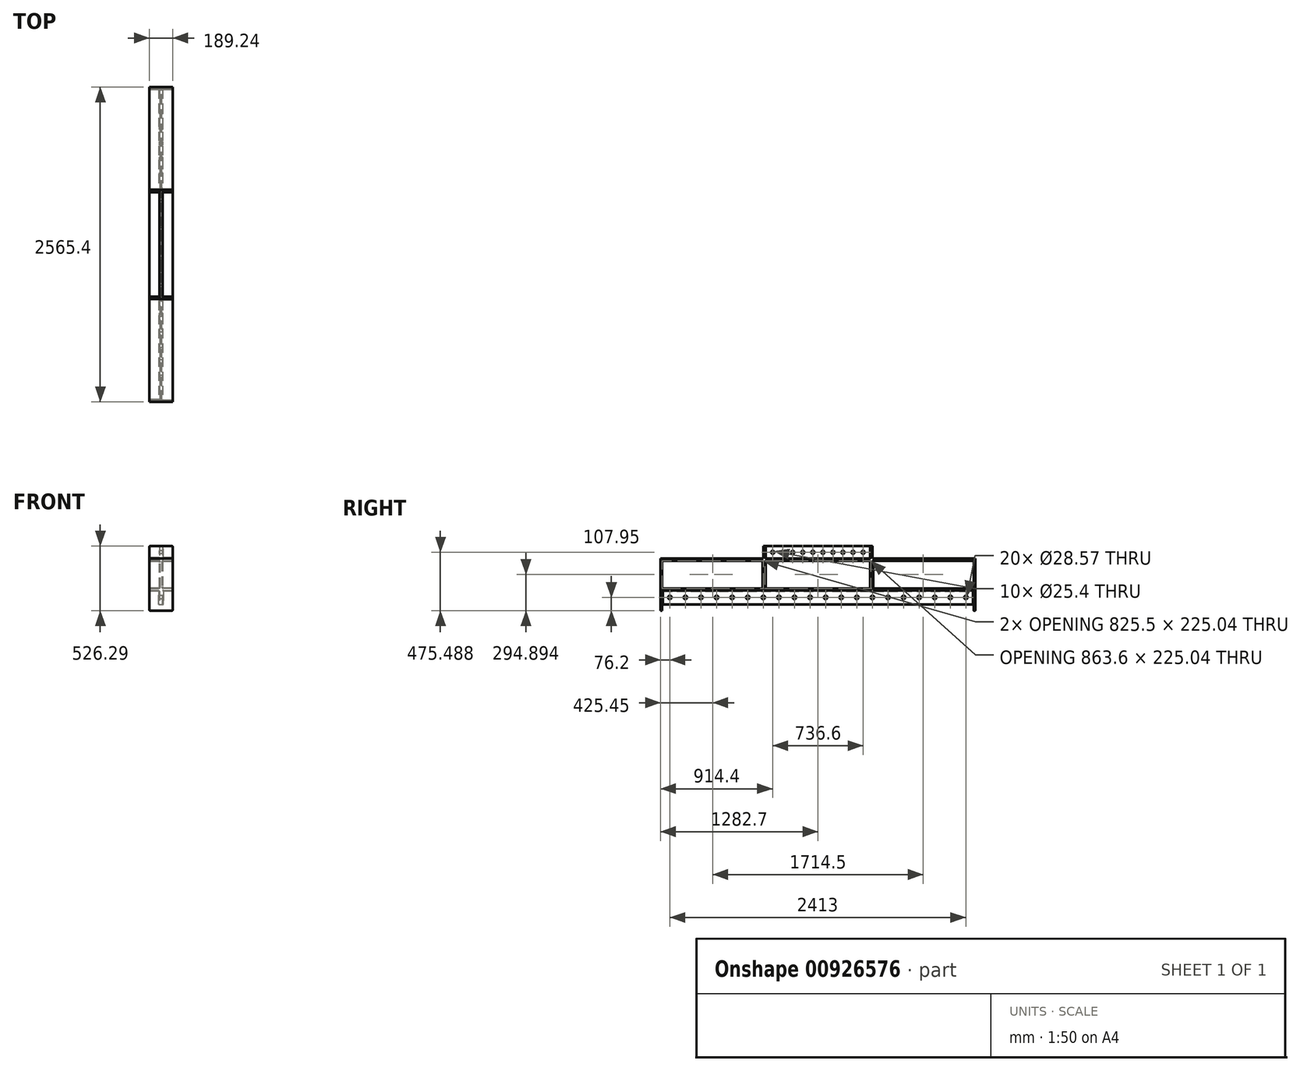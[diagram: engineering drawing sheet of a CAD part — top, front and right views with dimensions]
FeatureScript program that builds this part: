
annotation { "Feature Type Name" : "Feature", "Feature Type Description" : "" }
export const myFeature = defineFeature(function(context is Context, id is Id, definition is map)
    precondition{}
    {
        {
            var Q0;
            Q0=qCreatedBy(makeId("Front.planeOp"),FACE);
            var sketch = newSketch(context, id + "F0", { "sketchPlane" : qUnion([Q0])});
            skLineSegment(sketch, "E0", {"start": v(0, 0) * mm, "end": v(0, 259.59) * mm, "construction": true});
            skLineSegment(sketch, "E1", {"start": v(-94.62, 0) * mm, "end": v(94.62, 0) * mm, "construction": true});
            skLineSegment(sketch, "E2", {"start": v(-94.61, 259.59) * mm, "end": v(94.61, 259.59) * mm, "construction": true});
            skLineSegment(sketch, "E3", {"start": v(-94.61, 259.59) * mm, "end": v(94.61, 259.59) * mm});
            skLineSegment(sketch, "E4", {"start": v(-94.62, 0) * mm, "end": v(94.62, 0) * mm});
            skLineSegment(sketch, "E5", {"start": v(94.62, 17.27) * mm, "end": v(94.62, 0) * mm});
            skLineSegment(sketch, "E6", {"start": v(-94.62, 0) * mm, "end": v(-94.62, 17.27) * mm});
            skLineSegment(sketch, "E7", {"start": v(-94.61, 259.59) * mm, "end": v(-94.61, 242.32) * mm});
            skLineSegment(sketch, "E8", {"start": v(94.62, 259.59) * mm, "end": v(94.62, 242.32) * mm});
            skLineSegment(sketch, "E9", {"start": v(-94.62, 242.32) * mm, "end": v(-18.22, 242.32) * mm});
            skLineSegment(sketch, "E10", {"start": v(94.62, 242.32) * mm, "end": v(18.22, 242.32) * mm});
            skLineSegment(sketch, "E11", {"start": v(94.62, 17.27) * mm, "end": v(18.22, 17.27) * mm});
            skLineSegment(sketch, "E12", {"start": v(-94.62, 17.27) * mm, "end": v(-18.22, 17.27) * mm});
            skLineSegment(sketch, "E13", {"start": v(-5.33, 229.43) * mm, "end": v(-5.33, 30.16) * mm});
            skLineSegment(sketch, "E14", {"start": v(5.33, 229.43) * mm, "end": v(5.33, 30.16) * mm});
            skLineSegment(sketch, "E15", {"start": v(-5.33, 242.32) * mm, "end": v(5.33, 242.32) * mm, "construction": true});
            skPoint(sketch, "E16", {"position": v(0, 242.32) * mm});
            skPoint(sketch, "E17.visualSharp", {"position": v(-5.33, 242.32) * mm});
            skArc(sketch, "E17.filletArc", {"start": v(-5.33, 229.43) * mm, "mid": v(-9.1, 238.54) * mm, "end": v(-18.22, 242.32) * mm});
            skPoint(sketch, "E18.visualSharp", {"position": v(5.33, 242.32) * mm});
            skArc(sketch, "E18.filletArc", {"start": v(18.22, 242.32) * mm, "mid": v(9.1, 238.54) * mm, "end": v(5.33, 229.43) * mm});
            skPoint(sketch, "E19.visualSharp", {"position": v(5.33, 17.27) * mm});
            skArc(sketch, "E19.filletArc", {"start": v(5.33, 30.16) * mm, "mid": v(9.1, 21.05) * mm, "end": v(18.22, 17.27) * mm});
            skPoint(sketch, "E20.visualSharp", {"position": v(-5.33, 17.27) * mm});
            skArc(sketch, "E20.filletArc", {"start": v(-18.22, 17.27) * mm, "mid": v(-9.1, 21.05) * mm, "end": v(-5.33, 30.16) * mm});
            skSolve(sketch);
        }
        {
            var Q0;
            Q0=makeQuery(id+"F0.imprint","IMPRINT",FACE,{"disambiguationData":[TD([[makeQuery(id+"F0.imprint","IMPRINT",EDGE,{"derivedFrom":sQuery(id+"F0.wireOp",EDGE,"E3")}),-1.0]])]});
            extrude(context, id + "F1", {"entities" : qUnion([Q0]), "depth" : 2540 * mm, "offsetDistance" : 25.4 * mm});
        }
        {
            var Q0;
            Q0=qCreatedBy(makeId("Right.planeOp"),FACE);
            var sketch = newSketch(context, id + "F2", { "sketchPlane" : qUnion([Q0])});
            skPoint(sketch, "E21.0", {"position": v(-1270, 259.59) * mm});
            skLineSegment(sketch, "E22", {"start": v(-1270, 259.59) * mm, "end": v(-1270, 361.19) * mm, "construction": true});
            skLineSegment(sketch, "E23", {"start": v(-838.2, 361.19) * mm, "end": v(-1701.8, 361.19) * mm});
            skPoint(sketch, "E24", {"position": v(-1270, 310.39) * mm});
            skLineSegment(sketch, "E25", {"start": v(-838.2, 361.19) * mm, "end": v(-838.2, 259.59) * mm});
            skLineSegment(sketch, "E26", {"start": v(-838.2, 259.59) * mm, "end": v(-1701.8, 259.59) * mm});
            skLineSegment(sketch, "E27", {"start": v(-1701.8, 259.59) * mm, "end": v(-1701.8, 361.19) * mm});
            skPoint(sketch, "E28.visualSharp", {"position": v(-1701.8, 361.19) * mm});
            skPoint(sketch, "E29.visualSharp", {"position": v(-838.2, 361.19) * mm});
            skLineSegment(sketch, "E30", {"start": v(-901.7, 310.39) * mm, "end": v(-1638.3, 310.39) * mm, "construction": true});
            skCircle(sketch, "E31", {"center": v(-901.7, 310.39) * mm, "radius": 12.7 * mm});
            skCircle(sketch, "E32.1.0.0", {"center": v(-983.54, 310.39) * mm, "radius": 12.7 * mm});
            skCircle(sketch, "E32.2.0.0", {"center": v(-1065.39, 310.39) * mm, "radius": 12.7 * mm});
            skCircle(sketch, "E32.3.0.0", {"center": v(-1147.23, 310.39) * mm, "radius": 12.7 * mm});
            skCircle(sketch, "E32.4.0.0", {"center": v(-1229.08, 310.39) * mm, "radius": 12.7 * mm});
            skCircle(sketch, "E32.5.0.0", {"center": v(-1310.92, 310.39) * mm, "radius": 12.7 * mm});
            skCircle(sketch, "E32.6.0.0", {"center": v(-1392.77, 310.39) * mm, "radius": 12.7 * mm});
            skCircle(sketch, "E32.7.0.0", {"center": v(-1474.61, 310.39) * mm, "radius": 12.7 * mm});
            skCircle(sketch, "E32.8.0.0", {"center": v(-1556.46, 310.39) * mm, "radius": 12.7 * mm});
            skCircle(sketch, "E32.9.0.0", {"center": v(-1638.3, 310.39) * mm, "radius": 12.7 * mm});
            skLineSegment(sketch, "E32.direction1", {"start": v(-901.7, 310.39) * mm, "end": v(-983.54, 310.39) * mm, "construction": true});
            skLineSegment(sketch, "E33", {"start": v(-901.7, 310.39) * mm, "end": v(-901.7, 323.09) * mm, "construction": true});
            skSolve(sketch);
        }
        {
            var Q0;
            Q0=makeQuery(id+"F2.imprint","IMPRINT",FACE,{"disambiguationData":[TD([[makeQuery(id+"F2.imprint","IMPRINT",EDGE,{"derivedFrom":sQuery(id+"F2.wireOp",EDGE,"E23")}),1.0]])]});
            extrude(context, id + "F3", {"entities" : qUnion([Q0]), "operationType" : NewBodyOperationType.ADD, "depth" : 12.7 * mm, "offsetDistance" : 25.4 * mm, "hasSecondDirection" : true, "secondDirectionOppositeDirection" : true, "secondDirectionDepth" : 12.7 * mm});
        }
        {
            var Q0;
            Q0=qCreatedBy(makeId("Right.planeOp"),FACE);
            var sketch = newSketch(context, id + "F4", { "sketchPlane" : qUnion([Q0])});
            skLineSegment(sketch, "E34.0", {"start": v(-2540, 0) * mm, "end": v(0, 0) * mm});
            skLineSegment(sketch, "E35", {"start": v(0, 0) * mm, "end": v(0, -114.3) * mm});
            skLineSegment(sketch, "E36", {"start": v(-2540, 0) * mm, "end": v(-2540, -114.3) * mm});
            skLineSegment(sketch, "E37", {"start": v(0, -114.3) * mm, "end": v(-2540, -114.3) * mm});
            skLineSegment(sketch, "E38", {"start": v(0, -57.15) * mm, "end": v(-2540, -57.15) * mm, "construction": true});
            skCircle(sketch, "E39", {"center": v(-63.5, -57.15) * mm, "radius": 14.29 * mm});
            skLineSegment(sketch, "E40", {"start": v(-63.5, -57.15) * mm, "end": v(-63.5, -71.44) * mm, "construction": true});
            skCircle(sketch, "E41.1.0.0", {"center": v(-190.5, -57.15) * mm, "radius": 14.29 * mm});
            skCircle(sketch, "E41.2.0.0", {"center": v(-317.5, -57.15) * mm, "radius": 14.29 * mm});
            skCircle(sketch, "E41.3.0.0", {"center": v(-444.5, -57.15) * mm, "radius": 14.29 * mm});
            skCircle(sketch, "E41.4.0.0", {"center": v(-571.5, -57.15) * mm, "radius": 14.29 * mm});
            skCircle(sketch, "E41.5.0.0", {"center": v(-698.5, -57.15) * mm, "radius": 14.29 * mm});
            skCircle(sketch, "E41.6.0.0", {"center": v(-825.5, -57.15) * mm, "radius": 14.29 * mm});
            skCircle(sketch, "E41.7.0.0", {"center": v(-952.5, -57.15) * mm, "radius": 14.29 * mm});
            skCircle(sketch, "E41.8.0.0", {"center": v(-1079.5, -57.15) * mm, "radius": 14.29 * mm});
            skCircle(sketch, "E41.9.0.0", {"center": v(-1206.5, -57.15) * mm, "radius": 14.29 * mm});
            skCircle(sketch, "E41.10.0.0", {"center": v(-1333.5, -57.15) * mm, "radius": 14.29 * mm});
            skCircle(sketch, "E41.11.0.0", {"center": v(-1460.5, -57.15) * mm, "radius": 14.29 * mm});
            skCircle(sketch, "E41.12.0.0", {"center": v(-1587.5, -57.15) * mm, "radius": 14.29 * mm});
            skCircle(sketch, "E41.13.0.0", {"center": v(-1714.5, -57.15) * mm, "radius": 14.29 * mm});
            skCircle(sketch, "E41.14.0.0", {"center": v(-1841.5, -57.15) * mm, "radius": 14.29 * mm});
            skCircle(sketch, "E41.15.0.0", {"center": v(-1968.5, -57.15) * mm, "radius": 14.29 * mm});
            skCircle(sketch, "E41.16.0.0", {"center": v(-2095.5, -57.15) * mm, "radius": 14.29 * mm});
            skCircle(sketch, "E41.17.0.0", {"center": v(-2222.5, -57.15) * mm, "radius": 14.29 * mm});
            skCircle(sketch, "E41.18.0.0", {"center": v(-2349.5, -57.15) * mm, "radius": 14.29 * mm});
            skCircle(sketch, "E41.19.0.0", {"center": v(-2476.5, -57.15) * mm, "radius": 14.29 * mm});
            skLineSegment(sketch, "E41.direction1", {"start": v(-63.5, -57.15) * mm, "end": v(-190.5, -57.15) * mm, "construction": true});
            skPoint(sketch, "E42.visualSharp", {"position": v(0, -114.3) * mm});
            skPoint(sketch, "E43.visualSharp", {"position": v(-2540, -114.3) * mm});
            skSolve(sketch);
        }
        {
            var Q0;
            Q0 = qSketchRegion(id + "F4", true);
            extrude(context, id + "F5", {"entities" : qUnion([Q0]), "operationType" : NewBodyOperationType.ADD, "depth" : 12.7 * mm, "offsetDistance" : 25.4 * mm, "hasSecondDirection" : true, "secondDirectionOppositeDirection" : true, "secondDirectionDepth" : 12.7 * mm});
        }
        {
            var Q0;
            Q0=makeQuery(id+"F5.boolean.opBoolean","MERGE",FACE,{"derivedFrom":[makeQuery(id+"F1.opExtrude","CAP_FACE",FACE,{"disambiguationData":[OSD([sQuery(id+"F0.wireOp",EDGE,"E3"),sQuery(id+"F0.wireOp",EDGE,"E4"),sQuery(id+"F0.wireOp",EDGE,"E5"),sQuery(id+"F0.wireOp",EDGE,"E6"),sQuery(id+"F0.wireOp",EDGE,"E7"),sQuery(id+"F0.wireOp",EDGE,"E8"),sQuery(id+"F0.wireOp",EDGE,"E9"),sQuery(id+"F0.wireOp",EDGE,"E10"),sQuery(id+"F0.wireOp",EDGE,"E11"),sQuery(id+"F0.wireOp",EDGE,"E12"),sQuery(id+"F0.wireOp",EDGE,"E13"),sQuery(id+"F0.wireOp",EDGE,"E14"),sQuery(id+"F0.wireOp",EDGE,"E17.filletArc"),sQuery(id+"F0.wireOp",EDGE,"E18.filletArc"),sQuery(id+"F0.wireOp",EDGE,"E19.filletArc"),sQuery(id+"F0.wireOp",EDGE,"E20.filletArc")])],"isStart":true}),makeQuery(id+"F5.opExtrude","SWEPT_FACE",FACE,{"disambiguationData":[OSD([sQuery(id+"F4.wireOp",EDGE,"E35")])]})]});
            var sketch = newSketch(context, id + "F6", { "sketchPlane" : qUnion([Q0])});
            skLineSegment(sketch, "E44.bottom", {"start": v(-94.61, 259.59) * mm, "end": v(94.61, 259.59) * mm});
            skLineSegment(sketch, "E44.top", {"start": v(-94.61, -114.3) * mm, "end": v(94.61, -114.3) * mm});
            skLineSegment(sketch, "E44.left", {"start": v(-94.61, 259.59) * mm, "end": v(-94.61, -114.3) * mm});
            skLineSegment(sketch, "E44.right", {"start": v(94.61, 259.59) * mm, "end": v(94.61, -114.3) * mm});
            skSolve(sketch);
        }
        {
            var Q0;
            {var subQ1=sQuery(id+"F4.wireOp",EDGE,"E35");var subQ2=makeQuery(id+"F5.opExtrude","CAP_EDGE",EDGE,{"disambiguationData":[OSD([subQ1])],"isStart":true});Q0=makeQuery(id+"F6.imprint","IMPRINT",FACE,{"disambiguationData":[TD([[makeQuery(id+"F6.imprint","IMPRINT",EDGE,{"derivedFrom":subQ2}),1.0]])]});}
            var Q1;
            {var subQ0=makeQuery(id+"F1.opExtrude","CAP_EDGE",EDGE,{"disambiguationData":[OSD([sQuery(id+"F0.wireOp",EDGE,"E10")])],"isStart":true});Q1=makeQuery(id+"F6.imprint","IMPRINT",FACE,{"disambiguationData":[TD([[makeQuery(id+"F6.imprint","IMPRINT",EDGE,{"derivedFrom":subQ0}),-1.0]])]});}
            var Q2;
            {var subQ1=makeQuery(id+"F1.opExtrude","CAP_EDGE",EDGE,{"disambiguationData":[OSD([sQuery(id+"F0.wireOp",EDGE,"E9")])],"isStart":true});Q2=makeQuery(id+"F6.imprint","IMPRINT",FACE,{"disambiguationData":[TD([[makeQuery(id+"F6.imprint","IMPRINT",EDGE,{"derivedFrom":subQ1}),1.0]])]});}
            var Q3;
            {var subQ46=sQuery(id+"F6.wireOp",EDGE,"E44.bottom");Q3=makeQuery(id+"F6.imprint","IMPRINT",FACE,{"disambiguationData":[TD([[makeQuery(id+"F6.imprint","IMPRINT",EDGE,{"derivedFrom":subQ46}),1.0]])]});}
            var Q4;
            {var subQ1=sQuery(id+"F4.wireOp",EDGE,"E35");var subQ2=makeQuery(id+"F5.opExtrude","CAP_EDGE",EDGE,{"disambiguationData":[OSD([subQ1])],"isStart":false});Q4=makeQuery(id+"F6.imprint","IMPRINT",FACE,{"disambiguationData":[TD([[makeQuery(id+"F6.imprint","IMPRINT",EDGE,{"derivedFrom":subQ2}),-1.0]])]});}
            extrude(context, id + "F7", {"entities" : qUnion([Q0, Q1, Q2, Q3, Q4]), "operationType" : NewBodyOperationType.ADD, "depth" : 12.7 * mm, "offsetDistance" : 25.4 * mm});
        }
        {
            var Q0;
            Q0=makeQuery(id+"F5.boolean.opBoolean","MERGE",FACE,{"derivedFrom":[makeQuery(id+"F1.opExtrude","CAP_FACE",FACE,{"disambiguationData":[OSD([sQuery(id+"F0.wireOp",EDGE,"E3"),sQuery(id+"F0.wireOp",EDGE,"E4"),sQuery(id+"F0.wireOp",EDGE,"E5"),sQuery(id+"F0.wireOp",EDGE,"E6"),sQuery(id+"F0.wireOp",EDGE,"E7"),sQuery(id+"F0.wireOp",EDGE,"E8"),sQuery(id+"F0.wireOp",EDGE,"E9"),sQuery(id+"F0.wireOp",EDGE,"E10"),sQuery(id+"F0.wireOp",EDGE,"E11"),sQuery(id+"F0.wireOp",EDGE,"E12"),sQuery(id+"F0.wireOp",EDGE,"E13"),sQuery(id+"F0.wireOp",EDGE,"E14"),sQuery(id+"F0.wireOp",EDGE,"E17.filletArc"),sQuery(id+"F0.wireOp",EDGE,"E18.filletArc"),sQuery(id+"F0.wireOp",EDGE,"E19.filletArc"),sQuery(id+"F0.wireOp",EDGE,"E20.filletArc")])],"isStart":false}),makeQuery(id+"F5.opExtrude","SWEPT_FACE",FACE,{"disambiguationData":[OSD([sQuery(id+"F4.wireOp",EDGE,"E36")])]})]});
            var sketch = newSketch(context, id + "F8", { "sketchPlane" : qUnion([Q0])});
            skLineSegment(sketch, "E45.bottom", {"start": v(-94.61, 259.59) * mm, "end": v(94.61, 259.59) * mm});
            skLineSegment(sketch, "E45.top", {"start": v(-94.61, -114.3) * mm, "end": v(94.61, -114.3) * mm});
            skLineSegment(sketch, "E45.left", {"start": v(-94.61, 259.59) * mm, "end": v(-94.61, -114.3) * mm});
            skLineSegment(sketch, "E45.right", {"start": v(94.61, 259.59) * mm, "end": v(94.61, -114.3) * mm});
            skSolve(sketch);
        }
        {
            var Q0;
            Q0 = qSketchRegion(id + "F8", true);
            extrude(context, id + "F9", {"entities" : qUnion([Q0]), "operationType" : NewBodyOperationType.ADD, "depth" : 12.7 * mm, "offsetDistance" : 25.4 * mm});
        }
        {
            var Q0;
            Q0=makeQuery(id+"F3.opExtrude","SWEPT_FACE",FACE,{"disambiguationData":[OSD([sQuery(id+"F2.wireOp",EDGE,"E27")])]});
            var sketch = newSketch(context, id + "F10", { "sketchPlane" : qUnion([Q0])});
            skLineSegment(sketch, "E46.bottom", {"start": v(-94.61, 361.19) * mm, "end": v(94.61, 361.19) * mm});
            skLineSegment(sketch, "E46.top", {"start": v(-94.61, 259.59) * mm, "end": v(94.61, 259.59) * mm});
            skLineSegment(sketch, "E46.left", {"start": v(-94.61, 361.19) * mm, "end": v(-94.61, 259.59) * mm});
            skLineSegment(sketch, "E46.right", {"start": v(94.61, 361.19) * mm, "end": v(94.61, 259.59) * mm});
            skSolve(sketch);
        }
        {
            var Q0;
            Q0 = qSketchRegion(id + "F10", true);
            var Q1;
            {var subQ2=sQuery(id+"F10.wireOp",EDGE,"E46.right");Q1=makeQuery(id+"F10.imprint","IMPRINT",FACE,{"disambiguationData":[TD([[makeQuery(id+"F10.imprint","IMPRINT",EDGE,{"derivedFrom":subQ2}),-1.0]])]});}
            extrude(context, id + "F11", {"entities" : qUnion([Q0, Q1]), "operationType" : NewBodyOperationType.ADD, "depth" : 12.7 * mm, "offsetDistance" : 25.4 * mm});
        }
        {
            var Q0;
            Q0=makeQuery(id+"F3.opExtrude","SWEPT_FACE",FACE,{"disambiguationData":[OSD([sQuery(id+"F2.wireOp",EDGE,"E25")])]});
            var sketch = newSketch(context, id + "F12", { "sketchPlane" : qUnion([Q0])});
            skLineSegment(sketch, "E47.0.1", {"start": v(12.7, 259.59) * mm, "end": v(94.61, 259.59) * mm});
            skLineSegment(sketch, "E47.0.2", {"start": v(94.61, 259.59) * mm, "end": v(94.61, 361.19) * mm});
            skLineSegment(sketch, "E47.0.3", {"start": v(94.61, 361.19) * mm, "end": v(12.7, 361.19) * mm});
            skLineSegment(sketch, "E47.1.0", {"start": v(-94.61, 259.59) * mm, "end": v(-12.7, 259.59) * mm});
            skLineSegment(sketch, "E47.1.2", {"start": v(-12.7, 361.19) * mm, "end": v(-94.61, 361.19) * mm});
            skLineSegment(sketch, "E47.1.3", {"start": v(-94.61, 361.19) * mm, "end": v(-94.61, 259.59) * mm});
            skLineSegment(sketch, "E48", {"start": v(-12.7, 361.19) * mm, "end": v(12.7, 361.19) * mm});
            skLineSegment(sketch, "E49", {"start": v(-12.7, 259.59) * mm, "end": v(12.7, 259.59) * mm});
            skSolve(sketch);
        }
        {
            var Q0;
            Q0 = qSketchRegion(id + "F12", true);
            extrude(context, id + "F13", {"entities" : qUnion([Q0]), "operationType" : NewBodyOperationType.ADD, "depth" : 12.7 * mm, "offsetDistance" : 25.4 * mm});
        }
        {
            var Q0;
            Q0=makeQuery(id+"F9.boolean.opBoolean","MERGE",FACE,{"derivedFrom":[makeQuery(id+"F7.boolean.opBoolean","MERGE",FACE,{"derivedFrom":[makeQuery(id+"F5.opExtrude","SWEPT_FACE",FACE,{"disambiguationData":[OSD([sQuery(id+"F4.wireOp",EDGE,"E37")])]}),makeQuery(id+"F7.opExtrude","SWEPT_FACE",FACE,{"disambiguationData":[OSD([sQuery(id+"F6.wireOp",EDGE,"E44.top")])]})]}),makeQuery(id+"F9.opExtrude","SWEPT_FACE",FACE,{"disambiguationData":[OSD([sQuery(id+"F8.wireOp",EDGE,"E45.top")])]})]});
            var sketch = newSketch(context, id + "F14", { "sketchPlane" : qUnion([Q0])});
            skLineSegment(sketch, "E50.0", {"start": v(94.61, -12.7) * mm, "end": v(-94.61, -12.7) * mm});
            skLineSegment(sketch, "E51.0", {"start": v(-94.61, -12.7) * mm, "end": v(-94.61, 0) * mm});
            skLineSegment(sketch, "E51.1", {"start": v(94.61, -12.7) * mm, "end": v(94.61, 0) * mm});
            skLineSegment(sketch, "E52", {"start": v(-94.61, 0) * mm, "end": v(94.61, 0) * mm});
            skLineSegment(sketch, "E53", {"start": v(-94.61, 2552.7) * mm, "end": v(94.61, 2552.7) * mm});
            skLineSegment(sketch, "E54", {"start": v(94.61, 2552.7) * mm, "end": v(94.61, 2540) * mm});
            skLineSegment(sketch, "E55", {"start": v(94.61, 2540) * mm, "end": v(-94.61, 2540) * mm});
            skLineSegment(sketch, "E56", {"start": v(-94.61, 2540) * mm, "end": v(-94.61, 2552.7) * mm});
            skSolve(sketch);
        }
        {
            var Q0;
            Q0 = qSketchRegion(id + "F14", true);
            extrude(context, id + "F15", {"entities" : qUnion([Q0]), "operationType" : NewBodyOperationType.ADD, "depth" : 50.8 * mm, "offsetDistance" : 25.4 * mm});
        }
        {
            var Q0;
            Q0=makeQuery(id+"F15.boolean.opBoolean","MERGE",FACE,{"derivedFrom":[makeQuery(id+"F13.boolean.opBoolean","MERGE",FACE,{"derivedFrom":[makeQuery(id+"F11.boolean.opBoolean","MERGE",FACE,{"derivedFrom":[makeQuery(id+"F9.boolean.opBoolean","MERGE",FACE,{"derivedFrom":[makeQuery(id+"F7.boolean.opBoolean","MERGE",FACE,{"derivedFrom":[makeQuery(id+"F1.opExtrude","SWEPT_FACE",FACE,{"disambiguationData":[OSD([sQuery(id+"F0.wireOp",EDGE,"E5")])]}),makeQuery(id+"F1.opExtrude","SWEPT_FACE",FACE,{"disambiguationData":[OSD([sQuery(id+"F0.wireOp",EDGE,"E8")])]}),makeQuery(id+"F7.opExtrude","SWEPT_FACE",FACE,{"disambiguationData":[OSD([sQuery(id+"F6.wireOp",EDGE,"E44.left")])]})]}),makeQuery(id+"F9.opExtrude","SWEPT_FACE",FACE,{"disambiguationData":[OSD([sQuery(id+"F8.wireOp",EDGE,"E45.right")])]})]}),makeQuery(id+"F11.opExtrude","SWEPT_FACE",FACE,{"disambiguationData":[OSD([sQuery(id+"F10.wireOp",EDGE,"E46.right")])]})]}),makeQuery(id+"F13.opExtrude","SWEPT_FACE",FACE,{"disambiguationData":[OSD([sQuery(id+"F12.wireOp",EDGE,"E47.1.3")])]})]}),makeQuery(id+"F15.opExtrude","SWEPT_FACE",FACE,{"disambiguationData":[OSD([sQuery(id+"F14.wireOp",EDGE,"E51.1")])]}),makeQuery(id+"F15.opExtrude","SWEPT_FACE",FACE,{"disambiguationData":[OSD([sQuery(id+"F14.wireOp",EDGE,"E54")])]})]});
            var sketch = newSketch(context, id + "F16", { "sketchPlane" : qUnion([Q0])});
            skLineSegment(sketch, "E57", {"start": v(-1714.5, 259.59) * mm, "end": v(-1714.5, 242.32) * mm, "construction": true});
            skLineSegment(sketch, "E58", {"start": v(-1701.8, 259.59) * mm, "end": v(-1701.8, 242.32) * mm, "construction": true});
            skLineSegment(sketch, "E59", {"start": v(-1714.5, 242.32) * mm, "end": v(-1701.8, 242.32) * mm});
            skLineSegment(sketch, "E60", {"start": v(-1701.8, 242.32) * mm, "end": v(-1701.8, 17.27) * mm});
            skLineSegment(sketch, "E61", {"start": v(-1701.8, 17.27) * mm, "end": v(-1714.5, 17.27) * mm});
            skLineSegment(sketch, "E62", {"start": v(-1714.5, 17.27) * mm, "end": v(-1714.5, 242.32) * mm});
            skLineSegment(sketch, "E63", {"start": v(-838.2, 259.59) * mm, "end": v(-838.2, 242.32) * mm, "construction": true});
            skLineSegment(sketch, "E64", {"start": v(-825.5, 259.59) * mm, "end": v(-825.5, 242.32) * mm});
            skLineSegment(sketch, "E65", {"start": v(-838.2, 242.32) * mm, "end": v(-825.5, 242.32) * mm});
            skLineSegment(sketch, "E66", {"start": v(-825.5, 242.32) * mm, "end": v(-825.5, 17.27) * mm});
            skLineSegment(sketch, "E67", {"start": v(-825.5, 17.27) * mm, "end": v(-838.2, 17.27) * mm});
            skLineSegment(sketch, "E68", {"start": v(-838.2, 17.27) * mm, "end": v(-838.2, 242.32) * mm});
            skSolve(sketch);
        }
        {
            var Q0;
            Q0 = qSketchRegion(id + "F16", true);
            extrude(context, id + "F17", {"entities" : qUnion([Q0]), "operationType" : NewBodyOperationType.ADD, "oppositeDirection" : true, "depth" : 189.23 * mm, "offsetDistance" : 25.4 * mm});
        }
        {
            var Q0;
            Q0=makeQuery(id+"F13.opExtrude","SWEPT_EDGE",EDGE,{"disambiguationData":[OSD([sQuery(id+"F12.wireOp",EDGE,"E47.0.2"),sQuery(id+"F12.wireOp",EDGE,"E47.0.3")])]});
            var Q1;
            Q1=makeQuery(id+"F13.opExtrude","SWEPT_EDGE",EDGE,{"disambiguationData":[OSD([sQuery(id+"F12.wireOp",EDGE,"E47.1.2"),sQuery(id+"F12.wireOp",EDGE,"E47.1.3")])]});
            var Q2;
            Q2=makeQuery(id+"F11.opExtrude","SWEPT_EDGE",EDGE,{"disambiguationData":[OSD([sQuery(id+"F10.wireOp",EDGE,"E46.bottom"),sQuery(id+"F10.wireOp",EDGE,"E46.right")])]});
            var Q3;
            Q3=makeQuery(id+"F11.opExtrude","SWEPT_EDGE",EDGE,{"disambiguationData":[OSD([sQuery(id+"F10.wireOp",EDGE,"E46.bottom"),sQuery(id+"F10.wireOp",EDGE,"E46.left")])]});
            fillet(context, id + "F18", {"entities" : qUnion([Q0, Q1, Q2, Q3]), "radius" : 6.35 * mm, "tangentPropagation" : true, "allowEdgeOverflow" : false});
        }
        {
            var Q0;
            Q0=makeQuery(id+"F15.opExtrude","CAP_EDGE",EDGE,{"disambiguationData":[OSD([sQuery(id+"F14.wireOp",EDGE,"E54")])],"isStart":false});
            var Q1;
            Q1=makeQuery(id+"F15.opExtrude","CAP_EDGE",EDGE,{"disambiguationData":[OSD([sQuery(id+"F14.wireOp",EDGE,"E56")])],"isStart":false});
            var Q2;
            Q2=makeQuery(id+"F15.opExtrude","CAP_EDGE",EDGE,{"disambiguationData":[OSD([sQuery(id+"F14.wireOp",EDGE,"E51.0")])],"isStart":false});
            var Q3;
            Q3=makeQuery(id+"F15.opExtrude","CAP_EDGE",EDGE,{"disambiguationData":[OSD([sQuery(id+"F14.wireOp",EDGE,"E51.1")])],"isStart":false});
            fillet(context, id + "F19", {"entities" : qUnion([Q0, Q1, Q2, Q3]), "radius" : 6.35 * mm, "tangentPropagation" : true, "allowEdgeOverflow" : false});
        }
        {
            var Q0;
            Q0=makeQuery(id+"F5.opExtrude","CAP_EDGE",EDGE,{"disambiguationData":[OSD([sQuery(id+"F4.wireOp",EDGE,"E34.0")])],"isStart":true});
            var Q1;
            Q1=makeQuery(id+"F5.opExtrude","CAP_EDGE",EDGE,{"disambiguationData":[OSD([sQuery(id+"F4.wireOp",EDGE,"E34.0")])],"isStart":false});
            var Q2;
            Q2=makeQuery(id+"F5.opExtrude","CAP_EDGE",EDGE,{"disambiguationData":[OSD([sQuery(id+"F4.wireOp",EDGE,"E35")])],"isStart":false});
            var Q3;
            Q3=makeQuery(id+"F5.opExtrude","CAP_EDGE",EDGE,{"disambiguationData":[OSD([sQuery(id+"F4.wireOp",EDGE,"E36")])],"isStart":false});
            var Q4;
            Q4=makeQuery(id+"F15.opExtrude","CAP_EDGE",EDGE,{"disambiguationData":[OSD([sQuery(id+"F14.wireOp",EDGE,"E55")])],"isStart":true});
            var Q5;
            Q5=makeQuery(id+"F5.opExtrude","CAP_EDGE",EDGE,{"disambiguationData":[OSD([sQuery(id+"F4.wireOp",EDGE,"E36")])],"isStart":true});
            var Q6;
            Q6=makeQuery(id+"F15.opExtrude","CAP_EDGE",EDGE,{"disambiguationData":[OSD([sQuery(id+"F14.wireOp",EDGE,"E52")])],"isStart":true});
            var Q7;
            Q7=makeQuery(id+"F5.opExtrude","CAP_EDGE",EDGE,{"disambiguationData":[OSD([sQuery(id+"F4.wireOp",EDGE,"E35")])],"isStart":true});
            var Q8;
            Q8=makeQuery(id+"F1.opExtrude","CAP_EDGE",EDGE,{"disambiguationData":[OSD([sQuery(id+"F0.wireOp",EDGE,"E14")])],"isStart":true});
            var Q9;
            {var subQ1=sQuery(id+"F0.wireOp",EDGE,"E6");var subQ2=sQuery(id+"F0.wireOp",EDGE,"E4");Q9=makeQuery(id+"F5.boolean.opBoolean","SPLIT",EDGE,{"disambiguationData":[TD([makeQuery(id+"F1.opExtrude","SWEPT_FACE",FACE,{"disambiguationData":[OSD([subQ1])]})])],"derivedFrom":makeQuery(id+"F1.opExtrude","CAP_EDGE",EDGE,{"disambiguationData":[OSD([subQ2])],"isStart":true})});}
            var Q10;
            {var subQ0=sQuery(id+"F0.wireOp",EDGE,"E5");var subQ1=sQuery(id+"F0.wireOp",EDGE,"E4");Q10=makeQuery(id+"F5.boolean.opBoolean","SPLIT",EDGE,{"disambiguationData":[TD([makeQuery(id+"F1.opExtrude","SWEPT_FACE",FACE,{"disambiguationData":[OSD([subQ0])]})])],"derivedFrom":makeQuery(id+"F1.opExtrude","CAP_EDGE",EDGE,{"disambiguationData":[OSD([subQ1])],"isStart":true})});}
            var Q11;
            Q11=makeQuery(id+"F1.opExtrude","CAP_EDGE",EDGE,{"disambiguationData":[OSD([sQuery(id+"F0.wireOp",EDGE,"E13")])],"isStart":true});
            var Q12;
            Q12=makeQuery(id+"F1.opExtrude","CAP_EDGE",EDGE,{"disambiguationData":[OSD([sQuery(id+"F0.wireOp",EDGE,"E14")])],"isStart":false});
            var Q13;
            Q13=makeQuery(id+"F1.opExtrude","CAP_EDGE",EDGE,{"disambiguationData":[OSD([sQuery(id+"F0.wireOp",EDGE,"E13")])],"isStart":false});
            var Q14;
            {var subQ0=sQuery(id+"F16.wireOp",EDGE,"E62");Q14=makeQuery(id+"F17.boolean.opBoolean","SPLIT",EDGE,{"disambiguationData":[topologyDisambiguationEdgeConnected([makeQuery(id+"F1.opExtrude","SWEPT_FACE",FACE,{"disambiguationData":[OSD([sQuery(id+"F0.wireOp",EDGE,"E12")])]})])],"derivedFrom":makeQuery(id+"F17.opExtrude","SWEPT_EDGE",EDGE,{"disambiguationData":[OSD([sQuery(id+"F0.wireOp",EDGE,"E5"),sQuery(id+"F0.wireOp",EDGE,"E11"),sQuery(id+"F16.wireOp",EDGE,"E61"),subQ0])]})});}
            var Q15;
            Q15=makeQuery(id+"F17.boolean.opBoolean","INTERSECT",EDGE,{"derivedFrom":[makeQuery(id+"F1.opExtrude","SWEPT_FACE",FACE,{"disambiguationData":[OSD([sQuery(id+"F0.wireOp",EDGE,"E13")])]}),makeQuery(id+"F17.opExtrude","SWEPT_FACE",FACE,{"disambiguationData":[OSD([sQuery(id+"F16.wireOp",EDGE,"E60")])]})]});
            var Q16;
            Q16=makeQuery(id+"F17.boolean.opBoolean","INTERSECT",EDGE,{"derivedFrom":[makeQuery(id+"F1.opExtrude","SWEPT_FACE",FACE,{"disambiguationData":[OSD([sQuery(id+"F0.wireOp",EDGE,"E13")])]}),makeQuery(id+"F17.opExtrude","SWEPT_FACE",FACE,{"disambiguationData":[OSD([sQuery(id+"F16.wireOp",EDGE,"E66")])]})]});
            var Q17;
            Q17=makeQuery(id+"F17.boolean.opBoolean","INTERSECT",EDGE,{"derivedFrom":[makeQuery(id+"F1.opExtrude","SWEPT_FACE",FACE,{"disambiguationData":[OSD([sQuery(id+"F0.wireOp",EDGE,"E13")])]}),makeQuery(id+"F17.opExtrude","SWEPT_FACE",FACE,{"disambiguationData":[OSD([sQuery(id+"F16.wireOp",EDGE,"E68")])]})]});
            var Q18;
            Q18=makeQuery(id+"F17.boolean.opBoolean","INTERSECT",EDGE,{"derivedFrom":[makeQuery(id+"F1.opExtrude","SWEPT_FACE",FACE,{"disambiguationData":[OSD([sQuery(id+"F0.wireOp",EDGE,"E14")])]}),makeQuery(id+"F17.opExtrude","SWEPT_FACE",FACE,{"disambiguationData":[OSD([sQuery(id+"F16.wireOp",EDGE,"E66")])]})]});
            var Q19;
            Q19=makeQuery(id+"F17.boolean.opBoolean","INTERSECT",EDGE,{"derivedFrom":[makeQuery(id+"F1.opExtrude","SWEPT_FACE",FACE,{"disambiguationData":[OSD([sQuery(id+"F0.wireOp",EDGE,"E14")])]}),makeQuery(id+"F17.opExtrude","SWEPT_FACE",FACE,{"disambiguationData":[OSD([sQuery(id+"F16.wireOp",EDGE,"E68")])]})]});
            var Q20;
            Q20=makeQuery(id+"F17.boolean.opBoolean","INTERSECT",EDGE,{"derivedFrom":[makeQuery(id+"F1.opExtrude","SWEPT_FACE",FACE,{"disambiguationData":[OSD([sQuery(id+"F0.wireOp",EDGE,"E14")])]}),makeQuery(id+"F17.opExtrude","SWEPT_FACE",FACE,{"disambiguationData":[OSD([sQuery(id+"F16.wireOp",EDGE,"E62")])]})]});
            var Q21;
            Q21=makeQuery(id+"F17.boolean.opBoolean","INTERSECT",EDGE,{"derivedFrom":[makeQuery(id+"F1.opExtrude","SWEPT_FACE",FACE,{"disambiguationData":[OSD([sQuery(id+"F0.wireOp",EDGE,"E14")])]}),makeQuery(id+"F17.opExtrude","SWEPT_FACE",FACE,{"disambiguationData":[OSD([sQuery(id+"F16.wireOp",EDGE,"E60")])]})]});
            var Q22;
            {var subQ1=sQuery(id+"F10.wireOp",EDGE,"E46.top");Q22=makeQuery(id+"F11.boolean.opBoolean","SPLIT",EDGE,{"disambiguationData":[TD([makeQuery(id+"F1.opExtrude","SWEPT_FACE",FACE,{"disambiguationData":[OSD([sQuery(id+"F0.wireOp",EDGE,"E5")])]})])],"derivedFrom":makeQuery(id+"F11.opExtrude","CAP_EDGE",EDGE,{"disambiguationData":[OSD([subQ1])],"isStart":true})});}
            var Q23;
            Q23=makeQuery(id+"F3.opExtrude","CAP_EDGE",EDGE,{"disambiguationData":[OSD([sQuery(id+"F2.wireOp",EDGE,"E26")])],"isStart":false});
            var Q24;
            {var subQ0=sQuery(id+"F12.wireOp",EDGE,"E49");var subQ2=sQuery(id+"F12.wireOp",EDGE,"E47.1.0");var subQ3=sQuery(id+"F12.wireOp",EDGE,"E47.0.1");Q24=makeQuery(id+"F13.boolean.opBoolean","SPLIT",EDGE,{"disambiguationData":[TD([makeQuery(id+"F1.opExtrude","SWEPT_FACE",FACE,{"disambiguationData":[OSD([sQuery(id+"F0.wireOp",EDGE,"E5")])]})])],"derivedFrom":makeQuery(id+"F13.opExtrude","CAP_EDGE",EDGE,{"disambiguationData":[OSD([subQ3,subQ2,subQ0])],"isStart":true})});}
            var Q25;
            Q25=makeQuery(id+"F13.opExtrude","CAP_EDGE",EDGE,{"disambiguationData":[OSD([sQuery(id+"F12.wireOp",EDGE,"E47.0.1"),sQuery(id+"F12.wireOp",EDGE,"E47.1.0"),sQuery(id+"F12.wireOp",EDGE,"E49")])],"isStart":false});
            var Q26;
            Q26=makeQuery(id+"F11.opExtrude","CAP_EDGE",EDGE,{"disambiguationData":[OSD([sQuery(id+"F10.wireOp",EDGE,"E46.top")])],"isStart":false});
            var Q27;
            Q27=makeQuery(id+"F3.opExtrude","CAP_EDGE",EDGE,{"disambiguationData":[OSD([sQuery(id+"F2.wireOp",EDGE,"E27")])],"isStart":false});
            var Q28;
            Q28=makeQuery(id+"F3.opExtrude","CAP_EDGE",EDGE,{"disambiguationData":[OSD([sQuery(id+"F2.wireOp",EDGE,"E25")])],"isStart":false});
            var Q29;
            Q29=makeQuery(id+"F3.opExtrude","CAP_EDGE",EDGE,{"disambiguationData":[OSD([sQuery(id+"F2.wireOp",EDGE,"E26")])],"isStart":true});
            var Q30;
            {var subQ1=sQuery(id+"F10.wireOp",EDGE,"E46.top");Q30=makeQuery(id+"F11.boolean.opBoolean","SPLIT",EDGE,{"disambiguationData":[TD([makeQuery(id+"F1.opExtrude","SWEPT_FACE",FACE,{"disambiguationData":[OSD([sQuery(id+"F0.wireOp",EDGE,"E6")])]})])],"derivedFrom":makeQuery(id+"F11.opExtrude","CAP_EDGE",EDGE,{"disambiguationData":[OSD([subQ1])],"isStart":true})});}
            var Q31;
            Q31=makeQuery(id+"F3.opExtrude","CAP_EDGE",EDGE,{"disambiguationData":[OSD([sQuery(id+"F2.wireOp",EDGE,"E27")])],"isStart":true});
            var Q32;
            {var subQ0=sQuery(id+"F12.wireOp",EDGE,"E49");var subQ1=sQuery(id+"F12.wireOp",EDGE,"E47.1.0");var subQ3=sQuery(id+"F12.wireOp",EDGE,"E47.0.1");Q32=makeQuery(id+"F13.boolean.opBoolean","SPLIT",EDGE,{"disambiguationData":[TD([makeQuery(id+"F1.opExtrude","SWEPT_FACE",FACE,{"disambiguationData":[OSD([sQuery(id+"F0.wireOp",EDGE,"E6")])]})])],"derivedFrom":makeQuery(id+"F13.opExtrude","CAP_EDGE",EDGE,{"disambiguationData":[OSD([subQ3,subQ1,subQ0])],"isStart":true})});}
            var Q33;
            Q33=makeQuery(id+"F3.opExtrude","CAP_EDGE",EDGE,{"disambiguationData":[OSD([sQuery(id+"F2.wireOp",EDGE,"E25")])],"isStart":true});
            chamfer(context, id + "F20", {"entities" : qUnion([Q0, Q1, Q2, Q3, Q4, Q5, Q6, Q7, Q8, Q9, Q10, Q11, Q12, Q13, Q14, Q15, Q16, Q17, Q18, Q19, Q20, Q21, Q22, Q23, Q24, Q25, Q26, Q27, Q28, Q29, Q30, Q31, Q32, Q33]), "width" : 6.35 * mm, "tangentPropagation" : true});
        }
    });
